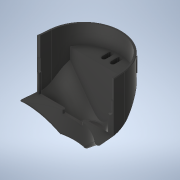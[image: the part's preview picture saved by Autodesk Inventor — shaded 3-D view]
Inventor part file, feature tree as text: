
AUTODESK INVENTOR PART (.ipt)
format: ipt  version: 2020.1 (Build 241239000, 239)  size: 4,183,552 bytes
history: native  units: mm
features: other x23, sketch x21, surface_op x16, extrude x11, projected_geometry x7, fillet x6, plane x4, emboss x3, delete_face x1, shell x1, loft x1
ambient origin geometry x8: Origin, YZ Plane, XZ Plane, XY Plane, X Axis, Y Axis, Z Axis, Center Point
bodies: Solid9 (feature_tree)
feature tree (94):
  other  "Bash Guard.ipt"
  sketch  "Sketch18"  dims[d14=2.75mm d15=2.75mm d26=64.0mm d170=52.0mm d171=2.0mm]
  plane  "Work Plane7"
  sketch  "Sketch19"  dims[d276=10.0mm d277=2.75mm d278=18.0mm]
  sketch  "Sketch20"  dims[d279=2.75mm d280=3.5mm]
  sketch  "3D Sketch6"
  plane  "Work Plane8"
  sketch  "Sketch21"  dims[d281=21.512mm d282=7.0mm]
  sketch  "Sketch22"  dims[d286=42.0mm d289=10.0mm]
  delete_face  "Delete Face7"
  sketch  "Sketch23"  dims[d290=0.0mm d291=0.0mm]
  surface_op  "Stitch Surface4"
  surface_op  "Stitch Surface5"
  surface_op  "Trim3"
  surface_op  "Trim4"
  surface_op  "Trim5"
  surface_op  "Extend2"
  surface_op  "Trim6"
  surface_op  "Extend3"
  surface_op  "Sculpt2"
  fillet  "Fillet7"  Radius=52.0mm
  sketch  "Sketch28"  dims[d299=2.75mm d300=17.0mm d301=2.0mm]
  extrude  "Extrusion19"  Depth=2.75mm
  shell  "Shell2"  Thickness=18.0mm
  extrude  "Extrusion20"  Depth=3.5mm
  extrude  "Extrusion21"  Depth=7.0mm
  extrude  "Extrusion22"  Depth=10.0mm
  extrude  "Extrusion23"  TaperAngle=0.0deg  [1 undecoded]
  extrude  "Extrusion24"  Depth=2.0mm
  fillet  "Fillet8"  Radius=2.75mm
  fillet  "Fillet9"  Radius=1.0mm
  extrude  "Extrusion25"  [1 undecoded]
  emboss  "Emboss1"
  plane  "Work Plane9"
  other  "Form7"
  surface_op  "Extend5"
  surface_op  "Sculpt4"
  extrude  "Extrusion26"  Depth=17.0mm
  fillet  "Fillet10"  Radius=2.0mm
  plane  "Work Plane10"
  sketch  "Sketch38"  dims[d331=4.25mm]
  extrude  "Extrusion27"  Depth=2.0mm
  fillet  "Fillet11"  [1 undecoded]
  fillet  "Fillet12"  [1 undecoded]
  emboss  "Emboss2"
  emboss  "Emboss3"
  other  "Holder::Bash Guard.ipt"
  other  "Holder Cover::Bash Guard.ipt"
  other  "TaggingFeature2"
  other  "3D Intersection1"
  other  "3D Intersection2"
  sketch  "3D Sketch7"
  other  "Srf7"
  other  "Srf8"
  other  "Srf11"
  sketch  "Sketch24"  dims[d292=-24.0mm d293=2.0mm d294=2.75mm d296=1.0mm]
  other  "Srf12"
  sketch  "3D Sketch8"
  other  "3D Intersection3"
  other  "Srf13"
  other  "Form6"
  surface_op  "Stitch Surface2"
  other  "Srf15"
  surface_op  "Stitch Surface3"
  other  "Srf16"
  other  "Srf17"
  other  "Srf18"
  sketch  "Sketch27"  dims[d297=2.0mm d298=-42.0mm]
  other  "Srf19"
  other  "Motor Cap"
  sketch  "Sketch29"  dims[d302=2.0mm d303=2.0mm d310=0.0mm d311=90.0deg d312=0.0mm d313=90.0deg]
  sketch  "Sketch30"  dims[d314=0.0mm d315=90.0deg d316=0.0mm d317=90.0deg]
  sketch  "Sketch31"  dims[d318=0.0mm d319=90.0deg d320=28.295mm d321=0.0mm]
  projected_geometry  "Projected Loop7"
  projected_geometry  "Projected Loop8"
  projected_geometry  "Projected Loop9"
  sketch  "Sketch35"  dims[d322=0.0mm d327=20.0mm d328=0.0mm]
  sketch  "Sketch36"  dims[d329=42.0mm]
  sketch  "Sketch37"  dims[d330=4.5mm]
  sketch  "Sketch39"  dims[d332=2.0mm]
  sketch  "Sketch40"  dims[d333=20.0mm d334=0.0mm d335=1.5mm d336=1.5mm d337=55.0mm d338=0.0mm d339=15.37mm d340=0.0mm d341=15.37mm d342=0.0mm d343=15.37mm d344=0.0mm d347=15.0mm d348=0.0mm d351=7.0mm d352=2.0mm d353=1.0mm d354=0.5mm d361=18.397mm d362=0.0mm d363=0.8mm d364=0.0mm d365=3.5mm d366=10.0mm d367=3.2mm d368=29.663794mm d369=3.0mm d371=3.0mm d372=0.0mm d374=15.0mm d375=2.0mm d376=0.4mm d377=0.0mm d378=0.4mm d379=0.0mm d380=3.5mm d381=9.0mm d382=0.0mm d383=1.25mm d384=1.25mm]
  projected_geometry  "Projected Loop12"
  projected_geometry  "Projected Loop13"
  projected_geometry  "Projected Loop14"
  projected_geometry  "Projected Loop15"
  loft  "LoftSrf1"
  extrude  "ExtrusionSrf2"  Depth=28.295mm TaperAngle=0.0deg
  extrude  "ExtrusionSrf3"  Depth=20.0mm TaperAngle=0.0deg
  surface_op  "Boundary Patch5"
  other  "Srf14"
  other  "Srf23"
  surface_op  "Boundary Patch3"
  surface_op  "Boundary Patch4"
  other  "Holder"
note: 4 required parameter values undecoded (feature->parameter linkage not recoverable at this tier; creation-order binding heuristic only, values carry confidence <= 0.55)
